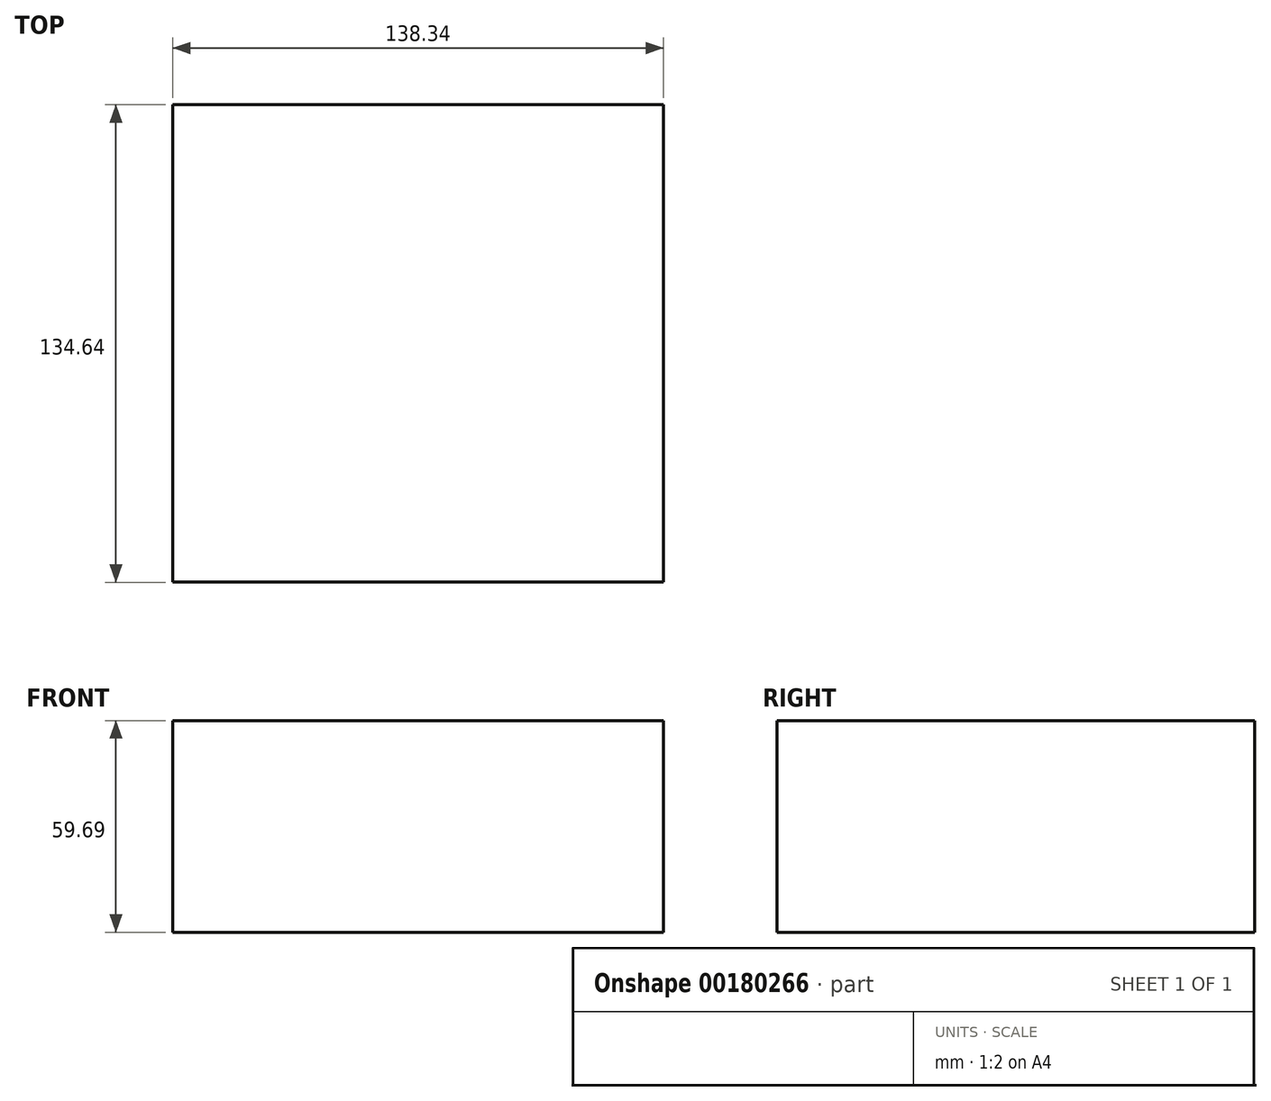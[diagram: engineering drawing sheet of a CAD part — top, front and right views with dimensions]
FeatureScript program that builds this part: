
annotation { "Feature Type Name" : "Feature", "Feature Type Description" : "" }
export const myFeature = defineFeature(function(context is Context, id is Id, definition is map)
    precondition{}
    {
        {
            var Q0;
            Q0=qCreatedBy(makeId("Top.planeOp"),FACE);
            var sketch = newSketch(context, id + "F0", { "sketchPlane" : qUnion([Q0])});
            skLineSegment(sketch, "E0.bottom", {"start": v(-69.6, 65.75) * mm, "end": v(68.74, 65.75) * mm});
            skLineSegment(sketch, "E0.top", {"start": v(-69.6, -68.89) * mm, "end": v(68.74, -68.89) * mm});
            skLineSegment(sketch, "E0.left", {"start": v(-69.6, 65.75) * mm, "end": v(-69.6, -68.89) * mm});
            skLineSegment(sketch, "E0.right", {"start": v(68.74, 65.75) * mm, "end": v(68.74, -68.89) * mm});
            skSolve(sketch);
        }
        {
            var Q0;
            Q0=makeQuery(id+"F0.imprint","IMPRINT",FACE,{"disambiguationData":[TD([[makeQuery(id+"F0.imprint","IMPRINT",EDGE,{"derivedFrom":sQuery(id+"F0.wireOp",EDGE,"E0.bottom")}),-1.0]])]});
            extrude(context, id + "F1", {"entities" : qUnion([Q0]), "depth" : 59.69 * mm});
        }
    });
